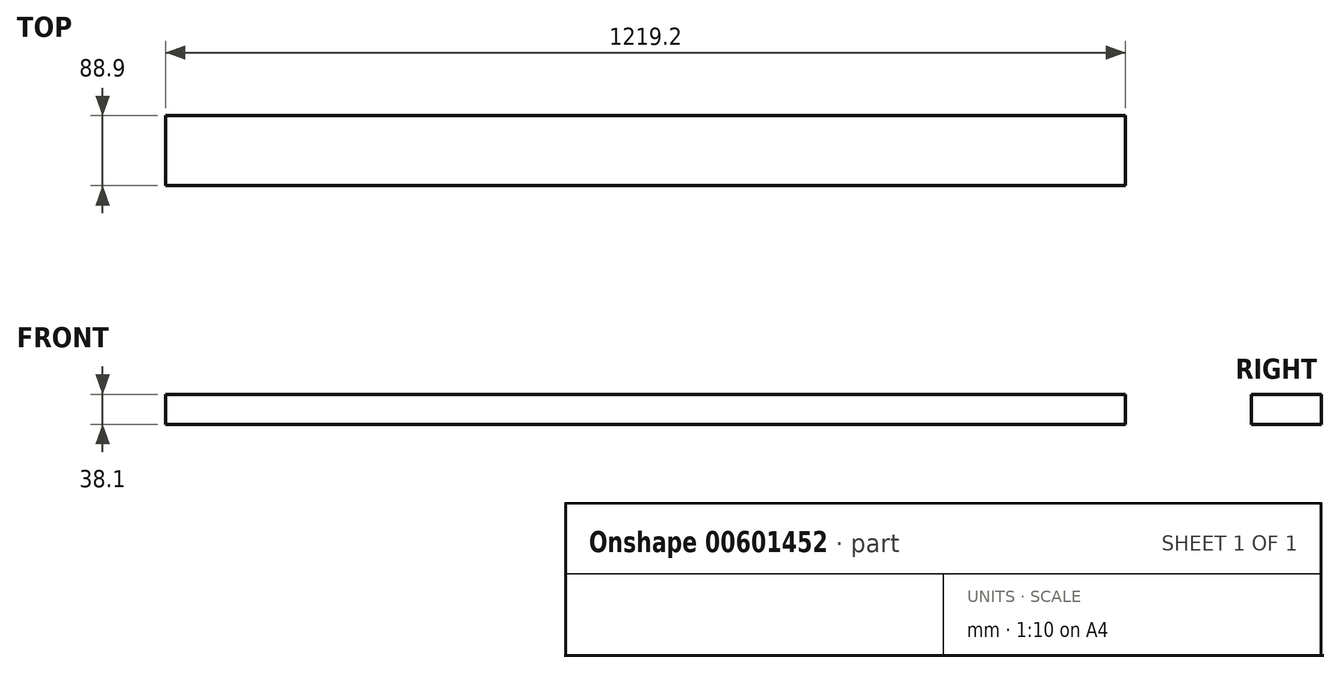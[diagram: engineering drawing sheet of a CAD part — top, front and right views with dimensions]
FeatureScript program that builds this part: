
annotation { "Feature Type Name" : "Feature", "Feature Type Description" : "" }
export const myFeature = defineFeature(function(context is Context, id is Id, definition is map)
    precondition{}
    {
        {
            var Q0;
            Q0=qCreatedBy(makeId("Top.planeOp"),FACE);
            var sketch = newSketch(context, id + "F0", { "sketchPlane" : qUnion([Q0])});
            skLineSegment(sketch, "E0.bottom", {"start": v(0, 0) * mm, "end": v(1219.2, 0) * mm});
            skLineSegment(sketch, "E0.top", {"start": v(0, 88.9) * mm, "end": v(1219.2, 88.9) * mm});
            skLineSegment(sketch, "E0.left", {"start": v(0, 0) * mm, "end": v(0, 88.9) * mm});
            skLineSegment(sketch, "E0.right", {"start": v(1219.2, 0) * mm, "end": v(1219.2, 88.9) * mm});
            skSolve(sketch);
        }
        {
            var Q0;
            Q0=qSketchRegion(id+"F0",true);
            extrude(context, id + "F1", {"entities" : qUnion([Q0]), "depth" : 38.1 * mm, "offsetDistance" : 25.4 * mm});
        }
    });
